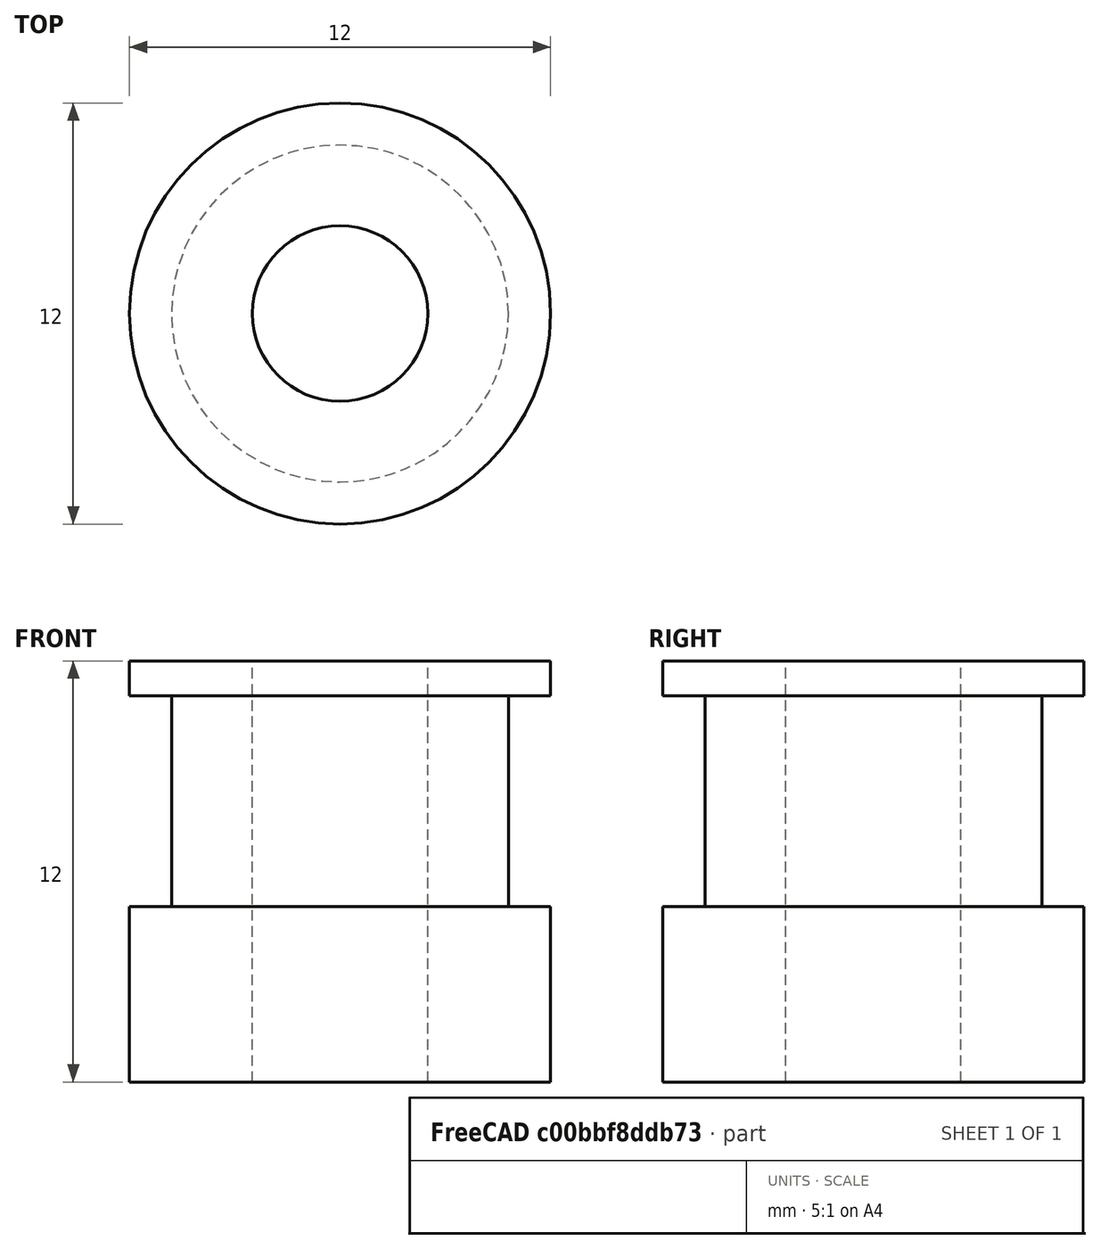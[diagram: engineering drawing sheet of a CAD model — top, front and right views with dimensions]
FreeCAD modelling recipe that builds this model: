
FCSTD DOCUMENT  (FreeCAD 0.18R14555 (Git shallow))
Label: pulley
License: All rights reserved
LicenseURL: http://en.wikipedia.org/wiki/All_rights_reserved
objects: Sketcher::SketchObject×1, PartDesign::Revolution×1, PartDesign::Body×1
note: 4 computed .brp shape members not serialized (recipe doc carries the construction recipe); baked Part::Feature solids carry a one-line shape summary decoded from their .brp

FEATURE [Sketcher::SketchObject] Sketch
  MapMode = 5
  Placement = pos=(0,0,0) rot=(1,0,0;1.5708rad)
  Support = -> [XZ_Plane]
  sketch-geometry (9):
    g0: LineSegment StartX=2.5 StartY=0 StartZ=0 EndX=2.5 EndY=12 EndZ=0
    g1: LineSegment StartX=2.5 StartY=12 StartZ=0 EndX=6 EndY=12 EndZ=0
    g2: LineSegment StartX=6 StartY=12 StartZ=0 EndX=6 EndY=11 EndZ=0
    g3: LineSegment StartX=6 StartY=11 StartZ=0 EndX=4.8 EndY=11 EndZ=0
    g4: LineSegment StartX=4.8 StartY=11 StartZ=0 EndX=4.8 EndY=5 EndZ=0
    g5: LineSegment StartX=4.8 StartY=5 StartZ=0 EndX=6 EndY=5 EndZ=0
    g6: LineSegment StartX=6 StartY=5 StartZ=0 EndX=6 EndY=0 EndZ=0
    g7: LineSegment StartX=6 StartY=0 StartZ=0 EndX=2.5 EndY=0 EndZ=0
    g8: LineSegment [constr] StartX=6 StartY=11 StartZ=0 EndX=6 EndY=5 EndZ=0
  constraints (26):
    c: Vertical(g0)
    c: Coincident(g0,g1)
    c: Horizontal(g1)
    c: Coincident(g1,g2)
    c: Vertical(g2)
    c: Coincident(g2,g3)
    c: Horizontal(g3)
    c: Coincident(g3,g4)
    c: Vertical(g4)
    c: Coincident(g4,g5)
    c: Horizontal(g5)
    c: Coincident(g5,g6)
    c: Vertical(g6)
    c: Coincident(g6,g7)
    c: Coincident(g7,g0)
    c: Horizontal(g7)
    c: PointOnObject(g0,g-1)
    c: DistanceX(g-1,g0) = 2.5
    c: DistanceX(g-1,g4) = 4.8
    c: DistanceX(g-1,g6) = 6
    c: DistanceY(g6,g6) = 5
    c: Coincident(g8,g2)
    c: Coincident(g8,g5)
    c: Vertical(g8)
    c: DistanceY(g2,g2) = 1
    c: DistanceY(g4,g4) = 6
FEATURE [PartDesign::Revolution] Revolution
  Angle = 360
  Axis = (0,2e-16,1)
  Base = (0,0,0)
  Placement = pos=(0,0,0) rot=(1,0,0;1.5708rad)
  Profile = -> Sketch
  ReferenceAxis = -> Sketch [V_Axis]
  Reversed = true
FEATURE [PartDesign::Body] Body
  Group = -> [Sketch,Revolution]
  Origin = -> Origin
  Tip = -> Revolution
